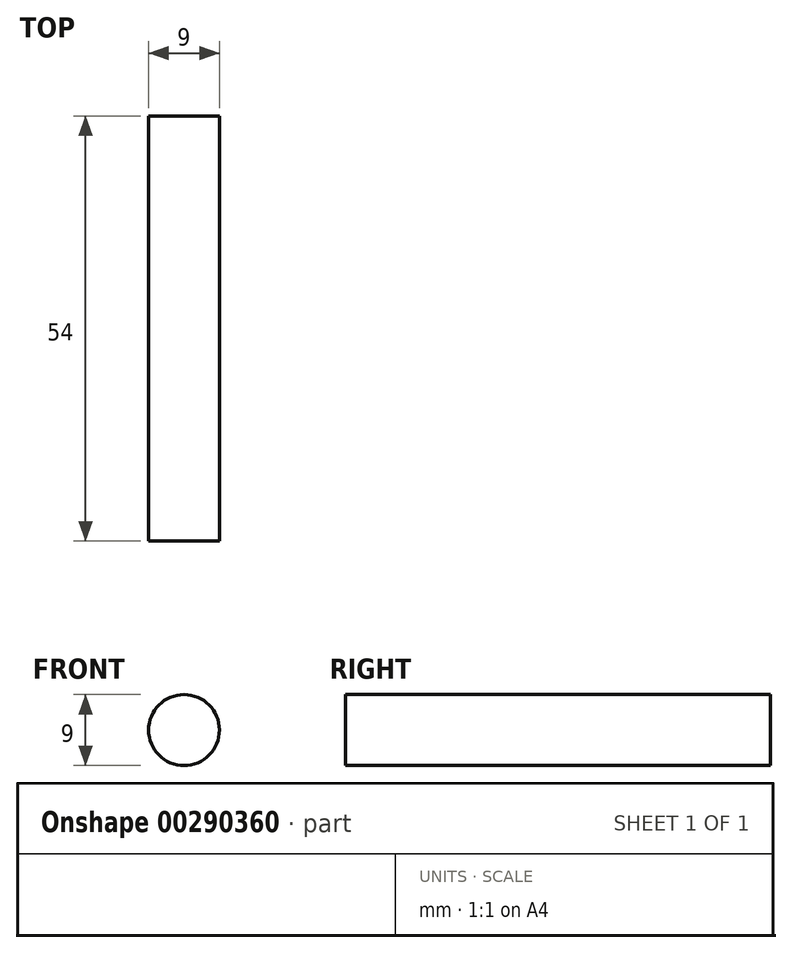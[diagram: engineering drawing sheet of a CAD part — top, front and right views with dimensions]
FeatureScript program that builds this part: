
annotation { "Feature Type Name" : "Feature", "Feature Type Description" : "" }
export const myFeature = defineFeature(function(context is Context, id is Id, definition is map)
    precondition{}
    {
        {
            var Q0;
            Q0=qCreatedBy(makeId("Front.planeOp"),FACE);
            var sketch = newSketch(context, id + "F0", { "sketchPlane" : qUnion([Q0])});
            skCircle(sketch, "E0", {"center": v(0, 0) * mm, "radius": 4.5 * mm});
            skSolve(sketch);
        }
        {
            var Q0;
            Q0=makeQuery(id+"F0.imprint","IMPRINT",FACE,{"disambiguationData":[TD([[makeQuery(id+"F0.imprint","IMPRINT",EDGE,{"derivedFrom":sQuery(id+"F0.wireOp",EDGE,"E0")}),1.0]])]});
            extrude(context, id + "F1", {"entities" : qUnion([Q0]), "depth" : 54 * mm});
        }
    });
